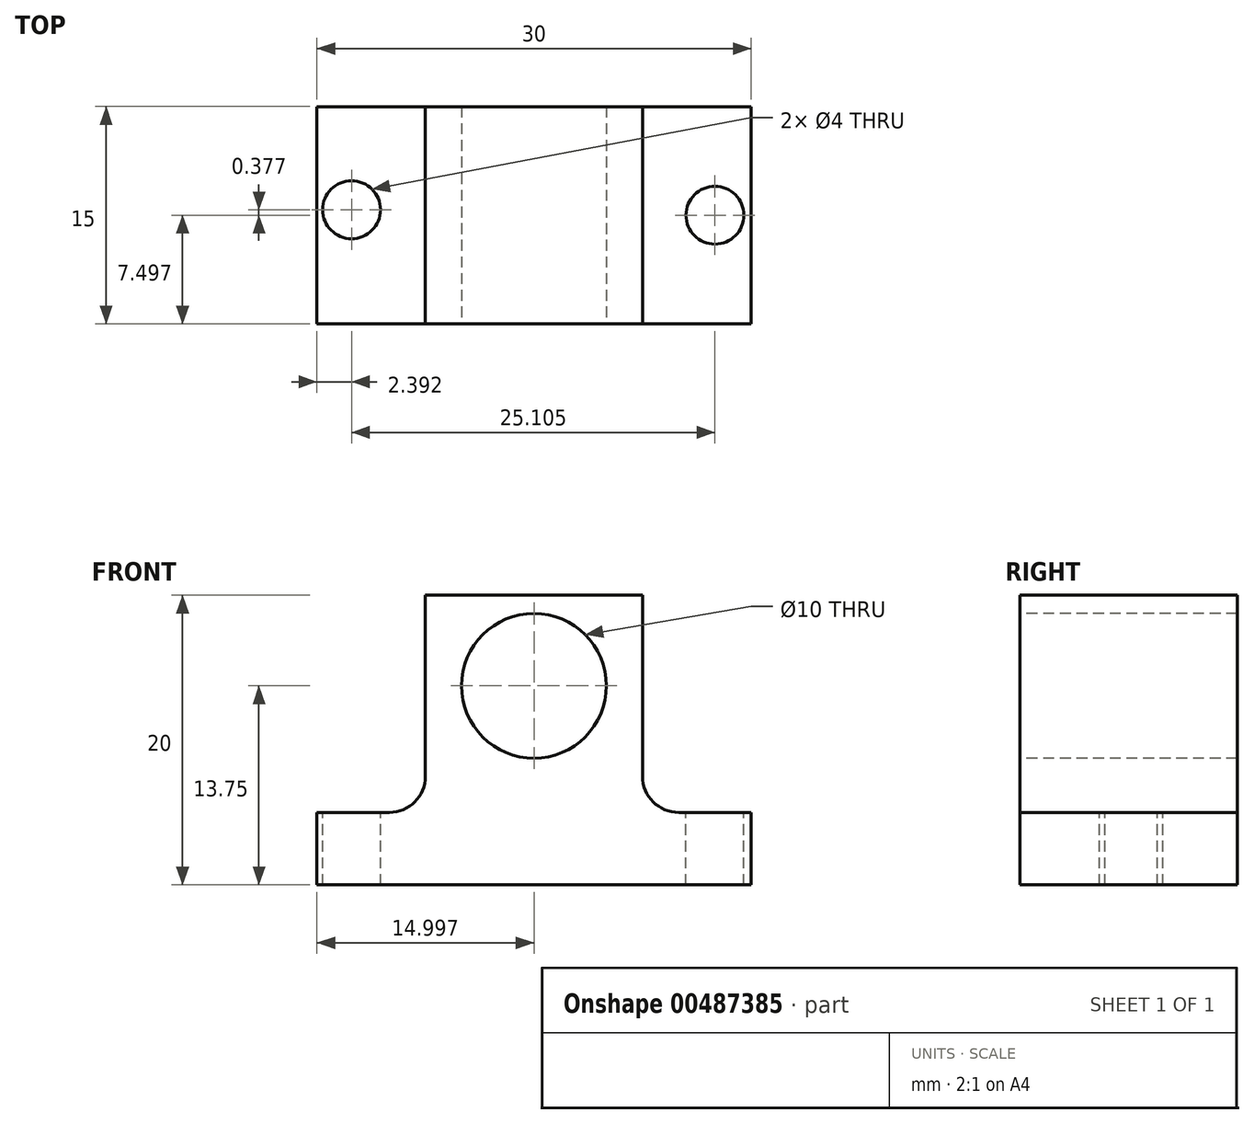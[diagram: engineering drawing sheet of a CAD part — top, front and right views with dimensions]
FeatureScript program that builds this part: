
annotation { "Feature Type Name" : "Feature", "Feature Type Description" : "" }
export const myFeature = defineFeature(function(context is Context, id is Id, definition is map)
    precondition{}
    {
        {
            var Q0;
            Q0=qCreatedBy(makeId("Top.planeOp"),FACE);
            var sketch = newSketch(context, id + "F0", { "sketchPlane" : qUnion([Q0])});
            skLineSegment(sketch, "E0.bottom", {"start": v(-8.77, -1.3) * mm, "end": v(21.23, -1.3) * mm});
            skLineSegment(sketch, "E0.top", {"start": v(-8.77, -16.3) * mm, "end": v(21.23, -16.3) * mm});
            skLineSegment(sketch, "E0.left", {"start": v(-8.77, -1.3) * mm, "end": v(-8.77, -16.3) * mm});
            skLineSegment(sketch, "E0.right", {"start": v(21.23, -1.3) * mm, "end": v(21.23, -16.3) * mm});
            skSolve(sketch);
        }
        {
            var Q0;
            Q0=makeQuery(id+"F0.imprint","IMPRINT",FACE,{"disambiguationData":[TD([[makeQuery(id+"F0.imprint","IMPRINT",EDGE,{"derivedFrom":sQuery(id+"F0.wireOp",EDGE,"E0.bottom")}),-1.0]])]});
            extrude(context, id + "F1", {"entities" : qUnion([Q0]), "depth" : 20 * mm});
        }
        {
            var Q0;
            Q0=makeQuery(id+"F1.opExtrude","SWEPT_FACE",FACE,{"disambiguationData":[OSD([sQuery(id+"F0.wireOp",EDGE,"E0.top")])]});
            var sketch = newSketch(context, id + "F2", { "sketchPlane" : qUnion([Q0])});
            skLineSegment(sketch, "E1", {"start": v(-8.77, 5) * mm, "end": v(-1.27, 5) * mm});
            skLineSegment(sketch, "E2", {"start": v(-1.27, 5) * mm, "end": v(-1.27, 20) * mm});
            skLineSegment(sketch, "E3", {"start": v(-1.27, 20) * mm, "end": v(13.73, 20) * mm});
            skLineSegment(sketch, "E4", {"start": v(13.73, 20) * mm, "end": v(13.73, 5) * mm});
            skLineSegment(sketch, "E5", {"start": v(13.73, 5) * mm, "end": v(21.23, 5) * mm});
            skSolve(sketch);
        }
        {
            var Q0;
            {var subQ0=sQuery(id+"F2.wireOp",EDGE,"E1");Q0=makeQuery(id+"F2.imprint","IMPRINT",FACE,{"disambiguationData":[TD([[makeQuery(id+"F2.imprint","IMPRINT",EDGE,{"derivedFrom":subQ0}),1.0]])]});}
            var Q1;
            {var subQ0=sQuery(id+"F2.wireOp",EDGE,"E4");Q1=makeQuery(id+"F2.imprint","IMPRINT",FACE,{"disambiguationData":[TD([[makeQuery(id+"F2.imprint","IMPRINT",EDGE,{"derivedFrom":subQ0}),1.0]])]});}
            extrude(context, id + "F3", {"entities" : qUnion([Q0, Q1]), "operationType" : NewBodyOperationType.REMOVE, "endBound" : BoundingType.THROUGH_ALL, "oppositeDirection" : true, "depth" : 25 * mm});
        }
        {
            var Q0;
            Q0=makeQuery(id+"F3.boolean.opBoolean","COPY",EDGE,{"derivedFrom":makeQuery(id+"F3.opExtrude","SWEPT_EDGE",EDGE,{"disambiguationData":[OSD([sQuery(id+"F2.wireOp",EDGE,"E4"),sQuery(id+"F2.wireOp",EDGE,"E5")])]})});
            var Q1;
            Q1=makeQuery(id+"F3.boolean.opBoolean","COPY",EDGE,{"derivedFrom":makeQuery(id+"F3.opExtrude","SWEPT_EDGE",EDGE,{"disambiguationData":[OSD([sQuery(id+"F2.wireOp",EDGE,"E1"),sQuery(id+"F2.wireOp",EDGE,"E2")])]})});
            fillet(context, id + "F4", {"entities" : qUnion([Q0, Q1]), "radius" : 2.5 * mm, "tangentPropagation" : true, "allowEdgeOverflow" : false});
        }
        {
            var Q0;
            Q0=makeQuery(id+"F1.opExtrude","SWEPT_FACE",FACE,{"disambiguationData":[OSD([sQuery(id+"F0.wireOp",EDGE,"E0.top")])]});
            var sketch = newSketch(context, id + "F5", { "sketchPlane" : qUnion([Q0])});
            skCircle(sketch, "E6", {"center": v(6.23, 13.75) * mm, "radius": 5 * mm});
            skSolve(sketch);
        }
        {
            var Q0;
            Q0=makeQuery(id+"F5.imprint","IMPRINT",FACE,{"disambiguationData":[TD([[makeQuery(id+"F5.imprint","IMPRINT",EDGE,{"derivedFrom":sQuery(id+"F5.wireOp",EDGE,"E6")}),1.0]])]});
            extrude(context, id + "F6", {"entities" : qUnion([Q0]), "operationType" : NewBodyOperationType.REMOVE, "endBound" : BoundingType.THROUGH_ALL, "oppositeDirection" : true, "depth" : 25 * mm});
        }
        {
            var Q0;
            Q0=makeQuery(id+"F3.boolean.opBoolean","COPY",FACE,{"derivedFrom":makeQuery(id+"F3.opExtrude","SWEPT_FACE",FACE,{"disambiguationData":[OSD([sQuery(id+"F2.wireOp",EDGE,"E5")])]})});
            var sketch = newSketch(context, id + "F7", { "sketchPlane" : qUnion([Q0])});
            skCircle(sketch, "E7", {"center": v(18.73, -8.8) * mm, "radius": 2 * mm});
            skCircle(sketch, "E8", {"center": v(-6.38, -8.43) * mm, "radius": 2 * mm});
            skSolve(sketch);
        }
        {
            var Q0;
            Q0=makeQuery(id+"F7.imprint","IMPRINT",FACE,{"disambiguationData":[TD([[makeQuery(id+"F7.imprint","IMPRINT",EDGE,{"derivedFrom":sQuery(id+"F7.wireOp",EDGE,"E8")}),1.0]])]});
            var Q1;
            Q1=makeQuery(id+"F7.imprint","IMPRINT",FACE,{"disambiguationData":[TD([[makeQuery(id+"F7.imprint","IMPRINT",EDGE,{"derivedFrom":sQuery(id+"F7.wireOp",EDGE,"E7")}),1.0]])]});
            extrude(context, id + "F8", {"entities" : qUnion([Q0, Q1]), "operationType" : NewBodyOperationType.REMOVE, "endBound" : BoundingType.THROUGH_ALL, "oppositeDirection" : true, "depth" : 25 * mm});
        }
    });
